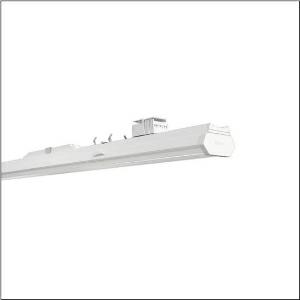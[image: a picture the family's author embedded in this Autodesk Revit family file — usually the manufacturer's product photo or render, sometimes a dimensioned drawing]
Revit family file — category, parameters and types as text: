
# Revit family: licross_r__21_protected_ho_52td12cn4cxm_6843
name_source: partatom
category: Lighting Fixtures
units: mm (PartAtom-declared; Revit-internal decimal feet)

## family parameters
Cut with Voids When Loaded = No
Host = Face
Light Source = No
Part Type = Normal
Room Calculation Point = No
Round Connector Dimension = Use Diameter
Shared = No

## types (1)
- --- (1 x LED, 12460 lm, 68.9 W, 4000K)
    Apparent Load = 69 VA
    CIE Flux Codes = 70 91 97 98 100
    Color Rendering = 80
    Color Temperature = 4000K
    Default Elevation = 1800 mm
    Description = Licross® 21 Protected HO, luminaire insert, of sheet steel, galvanised, coil coated, white, length: 1.500mm, width: 90mm, height: 103mm, LED rated luminous flux: 12.460lm, light colour: 840, control gear: ON/OFF Multilumen, CLOi, control gear: ECG Multilumen, with plug, 3-pole, with phase selection, mains connection: 220..240V, AC, 50/60Hz, start of lifetime: 69W, end of service life: 83W, internal wiring halogen-free, primary light control with lens, of plastic, primary optical cover: cover, of PMMA, light emission: direct distribution, primary light characteristic: symmetric, protection rating (complete): IP54, insulation class (complete): insulation class I (protective earthing), certification: CE, ENEC, VDE, UKCA, protection symbol: D if used in an environment with non-conductive dust loads with corresponding accessories, impact resistance: IK06, permissible ambient temperature for indoor applications: -35..+35°C, corresponds to IFS (International Featured Standards) requirements for safety and quality in the food industry, reducing of maximum allowable ambient temperature of 5°C with ceiling mounting, LABS conformity tested according to VDMA 24364:2018-05, packaging unit: 1 piece
    Height = 92 mm
    Lamp = 1 x LED
    Lamp Light Flux = 12460 lm
    Lamp Power = 68.9 W
    Lamp count = 1
    Length = 1500 mm
    Luminous efficacy = 181 lm/W
    Manufacturer = Siteco
    ModVariant = No
    Model = 52TD12CN4CXM
    Mounting Place = Ceiling
    Mounting Type = Pendant
    Number of Poles = 1
    OnlyDefault = Yes
    Power Factor = 1
    Product Name = Licross® 21 Protected HO
    Product group = luminaire insert | ceiling pendant
    ProductGroupID = 902
    Protection Class = Protection class I
    Protection Degree = IP 54
    RLX_Detail_Level = 1
    RLX_Emergency_Light_Flux = 0 lm
    RLX_Emergency_Type = 0
    RLX_Emergency_Type_DB = No
    RlxData = <blob elided: 22169 chars, md5=0815df70>
    Socket = socket
    Standby Power = 0 W
    System Light Flux = 12460 lm
    System Power = 69 W
    Type Comments = factory setting: luminous flux: 100 % | (A | C | E) | 162 mA
    Type Image = l_1256148.jpg
    URL = http://relux.com
    VarID = @adj_132979
    Voltage = 0 V
    Weight = 0.00 kg
    Width = 88 mm

## geometry (parser evidence)
native form markers: Blend x4, Sweep x12
no freeform markers — native parametric forms only
